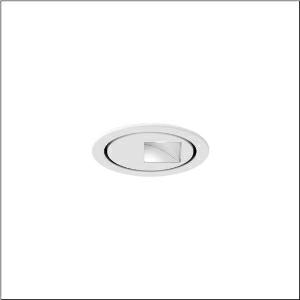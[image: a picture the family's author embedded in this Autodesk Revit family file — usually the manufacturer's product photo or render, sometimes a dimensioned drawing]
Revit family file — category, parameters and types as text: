
# Revit family: lunis_11_micro_round_51dj11cd1wg21
name_source: partatom
category: Lighting Fixtures
units: mm (PartAtom-declared; Revit-internal decimal feet)

## family parameters
Cut with Voids When Loaded = No
Host = Face
Light Source = No
Part Type = Normal
Room Calculation Point = No
Round Connector Dimension = Use Diameter
Shared = No

## types (1)
- Lunis 11 micro round (1 x LED 4000K / CRI = 80 (unbekannt), 1400 lm, 4000K)
    Apparent Load = 20 VA
    CIE Flux Codes = 42 75 96 100 100
    Color Rendering = 80
    Color Temperature = 4000K
    Default Elevation = 1800 mm
    Description = Lunis 11 micro round, downlight, light control with wallwasher, of highly reflective aluminium, highly specular, light emission: direct distribution, LED rated luminous flux: 1.400lm, light colour: 840, with terminal, 5-pole, mains connection: 220..230V, AC, 50/60Hz, LED module, of aluminium, highly specular, white, diameter: 114mm, clamping range: 1..40mm, recessing ring, of plastic, traffic white (RAL 9016), protection rating (complete): IP20, insulation class (complete): insulation class II (safety insulation), certification: CE, permissible ambient temperature for indoor applications: 0..+35°C, packaging unit: 1 piece
    Height = 0 mm  [stored 0 ft]
    Lamp = 1 x LED 4000K / CRI >= 80 (unbekannt)
    Lamp Light Flux = 1400 lm
    Lamp count = 1
    Length = 114 mm
    Luminous efficacy = 71 lm/W
    Manufacturer = Siteco
    ModVariant = No
    Model = 51DJ11CD1WG21
    Mounting Place = Ceiling
    Mounting Type = Recessed
    Number of Poles = 1
    OnlyDefault = Yes
    Power Factor = 1
    Product Name = Lunis 11 micro round
    Product group = downlight
    ProductGroupID = 400
    Protection Class = Protection class II
    Protection Degree = IP 20
    RLX_Detail_Level = 1
    RLX_Emergency_Light_Flux = 0 lm
    RLX_Emergency_Type = 0
    RLX_Emergency_Type_DB = No
    RlxData = <blob elided: 39945 chars, md5=fdf43f9d>
    Socket = socket
    Standby Power = 0 W
    System Light Flux = 1400 lm
    System Power = 20 W
    Type Comments = Product without accessories
    Type Image = l_1004773.jpg
    URL = http://relux.com
    VarID = ---
    Voltage = 0 V
    Weight = 0.00 kg
    Width = 114 mm

note: [stored X ft] marks values corroborated as IEEE doubles in the binary element streams (Revit-internal decimal feet)

## geometry (parser evidence)
native form markers: Blend x4, Sweep x9
no freeform markers — native parametric forms only
